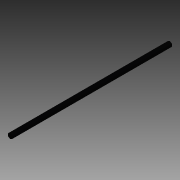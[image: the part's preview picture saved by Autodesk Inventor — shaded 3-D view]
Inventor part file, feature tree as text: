
AUTODESK INVENTOR PART (.ipt)
format: ipt  version: 2014 SP1 (Build 180222100, 222)  size: 69,632 bytes
history: native  units: in
note: dims shown in document units (in); Inventor stores cm internally (conversion verified against a paired STEP export)
features: extrude x1, sketch x1
ambient origin geometry x8: Origin, YZ Plane, XZ Plane, XY Plane, X Axis, Y Axis, Z Axis, Center Point
bodies: Solid1 (feature_tree)
feature tree (2):
  extrude  "Extrusion1"  Depth=18.0in TaperAngle=0.0deg
  sketch  "Sketch1"  dims[d0=0.5in d1=18.0in d2=0.0in]
